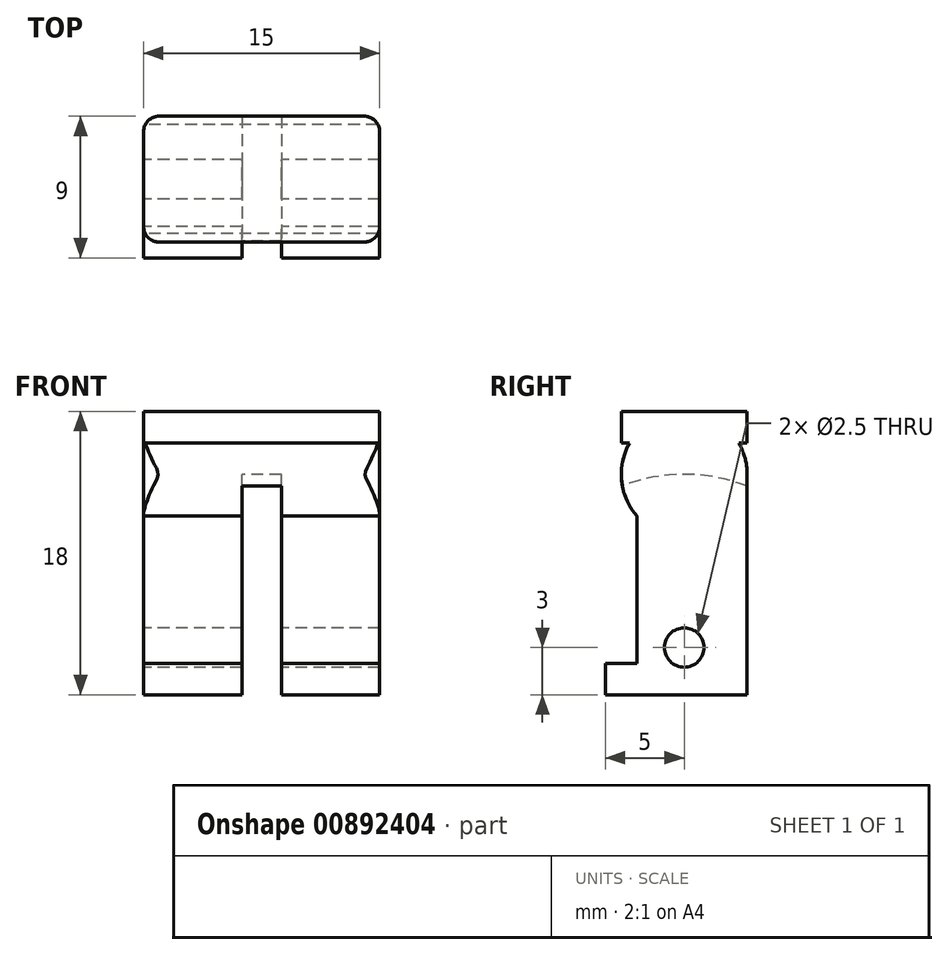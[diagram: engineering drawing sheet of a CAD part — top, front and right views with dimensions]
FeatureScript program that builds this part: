
annotation { "Feature Type Name" : "Feature", "Feature Type Description" : "" }
export const myFeature = defineFeature(function(context is Context, id is Id, definition is map)
    precondition{}
    {
        {
            var Q0;
            Q0=qCreatedBy(makeId("Right.planeOp"),FACE);
            var sketch = newSketch(context, id + "F0", { "sketchPlane" : qUnion([Q0])});
            skLineSegment(sketch, "E0.bottom", {"start": v(4, -1) * mm, "end": v(3.46, -1) * mm});
            skLineSegment(sketch, "E0.top", {"start": v(4, 1) * mm, "end": v(-4, 1) * mm});
            skLineSegment(sketch, "E0.left", {"start": v(4, -1) * mm, "end": v(4, 1) * mm});
            skLineSegment(sketch, "E0.right", {"start": v(-4, -1) * mm, "end": v(-4, 1) * mm});
            skPoint(sketch, "E0.middle", {"position": v(0, 0) * mm});
            skArc(sketch, "E1", {"start": v(-3.46, -1) * mm, "mid": v(-3.98, -3.4) * mm, "end": v(-3, -5.65) * mm});
            skLineSegment(sketch, "E2.left", {"start": v(4, -3) * mm, "end": v(4, -15) * mm});
            skLineSegment(sketch, "E2.right", {"start": v(-3, -5.65) * mm, "end": v(-3, -15) * mm});
            skLineSegment(sketch, "E3.top", {"start": v(4, -17) * mm, "end": v(-5, -17) * mm});
            skLineSegment(sketch, "E3.left", {"start": v(4, -15) * mm, "end": v(4, -17) * mm});
            skLineSegment(sketch, "E3.right", {"start": v(-5, -15) * mm, "end": v(-5, -17) * mm});
            skCircle(sketch, "E4", {"center": v(0, -14) * mm, "radius": 1.25 * mm});
            skLineSegment(sketch, "E5.trimOffspring", {"start": v(-3.46, -1) * mm, "end": v(-4, -1) * mm});
            skArc(sketch, "E6.trimOffspring", {"start": v(4, -3) * mm, "mid": v(3.86, -1.96) * mm, "end": v(3.46, -1) * mm});
            skLineSegment(sketch, "E7.trimOffspring", {"start": v(-3, -15) * mm, "end": v(-5, -15) * mm});
            skSolve(sketch);
        }
        {
            var Q0;
            Q0 = qSketchRegion(id + "F0", true);
            extrude(context, id + "F1", {"entities" : qUnion([Q0]), "endBound" : BoundingType.SYMMETRIC, "depth" : 15 * mm, "offsetDistance" : 25.4 * mm});
        }
        {
            var Q0;
            Q0=qCreatedBy(makeId("Right.planeOp"),FACE);
            var sketch = newSketch(context, id + "F2", { "sketchPlane" : qUnion([Q0])});
            skCircle(sketch, "E8", {"center": v(0, -14) * mm, "radius": 11 * mm});
            skSolve(sketch);
        }
        {
            var Q0;
            Q0 = qSketchRegion(id + "F2", true);
            extrude(context, id + "F3", {"entities" : qUnion([Q0]), "operationType" : NewBodyOperationType.REMOVE, "endBound" : BoundingType.SYMMETRIC, "depth" : 2.5 * mm, "offsetDistance" : 25.4 * mm});
        }
        {
            var Q0;
            Q0=makeQuery(id+"F1.opExtrude","CAP_EDGE",EDGE,{"disambiguationData":[OSD([sQuery(id+"F0.wireOp",EDGE,"E0.right")])],"isStart":false});
            fillet(context, id + "F4", {"entities" : qUnion([Q0]), "radius" : 1 * mm, "tangentPropagation" : true, "allowEdgeOverflow" : false});
        }
        {
            var Q0;
            Q0=makeQuery(id+"F1.opExtrude","CAP_EDGE",EDGE,{"disambiguationData":[OSD([sQuery(id+"F0.wireOp",EDGE,"E0.left")])],"isStart":false});
            fillet(context, id + "F5", {"entities" : qUnion([Q0]), "radius" : 1 * mm, "tangentPropagation" : true, "allowEdgeOverflow" : false});
        }
        {
            var Q0;
            Q0=makeQuery(id+"F1.opExtrude","CAP_EDGE",EDGE,{"disambiguationData":[OSD([sQuery(id+"F0.wireOp",EDGE,"E0.right")])],"isStart":true});
            fillet(context, id + "F6", {"entities" : qUnion([Q0]), "radius" : 1 * mm, "tangentPropagation" : true, "allowEdgeOverflow" : false});
        }
        {
            var Q0;
            Q0=makeQuery(id+"F1.opExtrude","CAP_EDGE",EDGE,{"disambiguationData":[OSD([sQuery(id+"F0.wireOp",EDGE,"E0.left")])],"isStart":true});
            fillet(context, id + "F7", {"entities" : qUnion([Q0]), "radius" : 1 * mm, "tangentPropagation" : true, "allowEdgeOverflow" : false});
        }
    });
